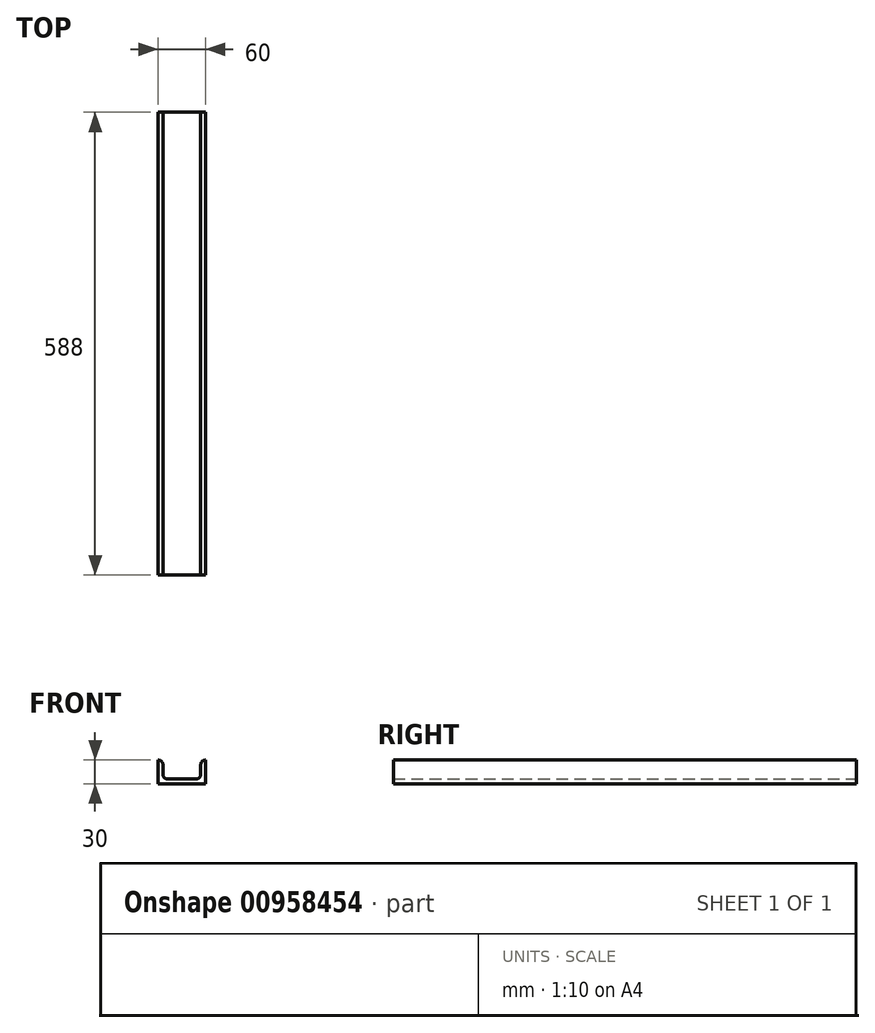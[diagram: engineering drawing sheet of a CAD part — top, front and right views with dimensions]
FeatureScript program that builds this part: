
annotation { "Feature Type Name" : "Feature", "Feature Type Description" : "" }
export const myFeature = defineFeature(function(context is Context, id is Id, definition is map)
    precondition{}
    {
        {
            var Q0;
            Q0=qCreatedBy(makeId("Front.planeOp"),FACE);
            var sketch = newSketch(context, id + "F0", { "sketchPlane" : qUnion([Q0])});
            skLineSegment(sketch, "E0", {"start": v(0, 0) * mm, "end": v(60, 0) * mm});
            skLineSegment(sketch, "E1", {"start": v(60, 0) * mm, "end": v(60, 30) * mm});
            skLineSegment(sketch, "E2", {"start": v(0, 0) * mm, "end": v(0, 30) * mm});
            skLineSegment(sketch, "E3.0", {"start": v(6, 12) * mm, "end": v(6, 24) * mm});
            skLineSegment(sketch, "E3.1", {"start": v(12, 6) * mm, "end": v(48, 6) * mm});
            skLineSegment(sketch, "E3.2", {"start": v(54, 12) * mm, "end": v(54, 24) * mm});
            skLineSegment(sketch, "E4", {"start": v(0, 30) * mm, "end": v(0, 30) * mm});
            skLineSegment(sketch, "E5", {"start": v(60, 30) * mm, "end": v(60, 30) * mm});
            skPoint(sketch, "E6.visualSharp", {"position": v(6, 30) * mm});
            skArc(sketch, "E6.filletArc", {"start": v(6, 24) * mm, "mid": v(4.24, 28.24) * mm, "end": v(0, 30) * mm});
            skPoint(sketch, "E7.visualSharp", {"position": v(54, 30) * mm});
            skArc(sketch, "E7.filletArc", {"start": v(60, 30) * mm, "mid": v(55.76, 28.24) * mm, "end": v(54, 24) * mm});
            skPoint(sketch, "E8.visualSharp", {"position": v(54, 6) * mm});
            skArc(sketch, "E8.filletArc", {"start": v(48, 6) * mm, "mid": v(52.24, 7.76) * mm, "end": v(54, 12) * mm});
            skPoint(sketch, "E9.visualSharp", {"position": v(6, 6) * mm});
            skArc(sketch, "E9.filletArc", {"start": v(6, 12) * mm, "mid": v(7.76, 7.76) * mm, "end": v(12, 6) * mm});
            skSolve(sketch);
        }
        {
            var Q0;
            Q0=makeQuery(id+"F0.imprint","IMPRINT",FACE,{"disambiguationData":[TD([[makeQuery(id+"F0.imprint","IMPRINT",EDGE,{"derivedFrom":sQuery(id+"F0.wireOp",EDGE,"E0")}),1.0]])]});
            extrude(context, id + "F1", {"entities" : qUnion([Q0]), "depth" : 588 * mm, "offsetDistance" : 25 * mm});
        }
    });
